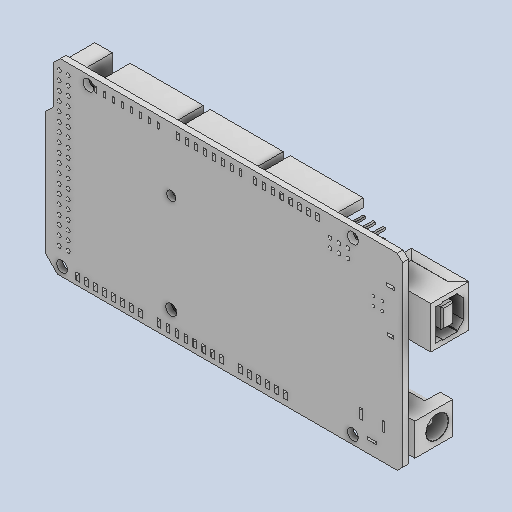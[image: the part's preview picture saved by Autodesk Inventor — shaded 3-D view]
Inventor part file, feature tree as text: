
AUTODESK INVENTOR PART (.ipt)
format: ipt  version: 2024.2 (Build 282272000, 272)  size: 1,235,456 bytes
history: native  units: in
note: dims shown in document units (in); Inventor stores cm internally (conversion verified against a paired STEP export)
features: fillet x1
ambient origin geometry x8: Origin, YZ Plane, XZ Plane, XY Plane, X Axis, Y Axis, Z Axis, Center Point
bodies: Solid1 (feature_tree)
feature tree (1):
  fillet  "Fillet5"  [1 undecoded]
note: 1 required parameter value undecoded (feature->parameter linkage not recoverable at this tier; creation-order binding heuristic only, values carry confidence <= 0.55)
